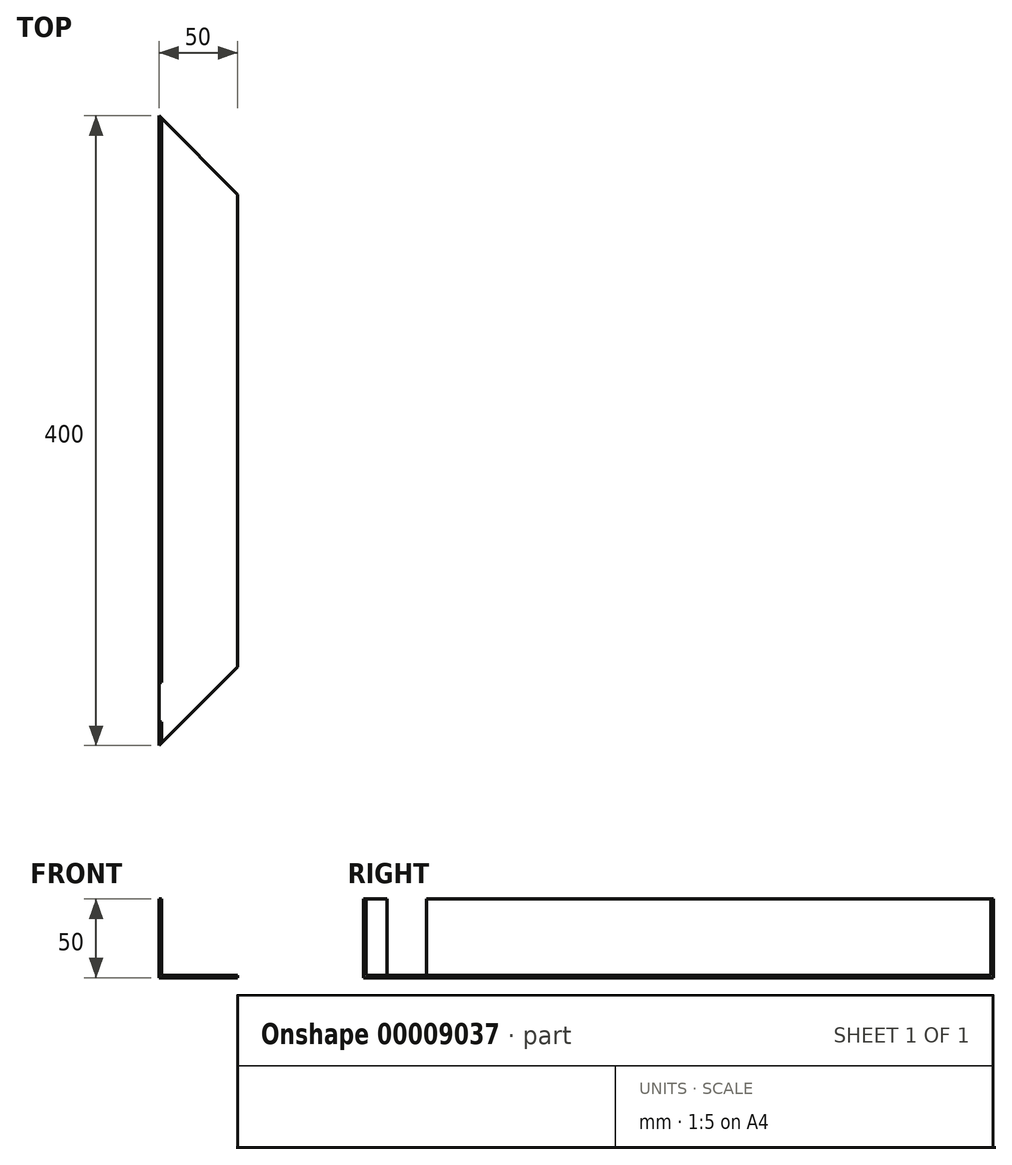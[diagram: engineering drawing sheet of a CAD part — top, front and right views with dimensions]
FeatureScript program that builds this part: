
annotation { "Feature Type Name" : "Feature", "Feature Type Description" : "" }
export const myFeature = defineFeature(function(context is Context, id is Id, definition is map)
    precondition{}
    {
        {
            var Q0;
            Q0=qCreatedBy(makeId("Front.planeOp"),FACE);
            var sketch = newSketch(context, id + "F0", { "sketchPlane" : qUnion([Q0])});
            skLineSegment(sketch, "E0.bottom", {"start": v(-33, 48.4) * mm, "end": v(-31.4, 48.4) * mm});
            skLineSegment(sketch, "E0.top", {"start": v(-33, -1.6) * mm, "end": v(-31.4, -1.6) * mm});
            skLineSegment(sketch, "E0.left", {"start": v(-33, 48.4) * mm, "end": v(-33, -1.6) * mm});
            skLineSegment(sketch, "E0.right", {"start": v(-31.4, 48.4) * mm, "end": v(-31.4, -1.6) * mm});
            skLineSegment(sketch, "E1.bottom", {"start": v(-33, -1.6) * mm, "end": v(17, -1.6) * mm});
            skLineSegment(sketch, "E1.top", {"start": v(-33, 0) * mm, "end": v(17, 0) * mm});
            skLineSegment(sketch, "E1.left", {"start": v(-33, -1.6) * mm, "end": v(-33, 0) * mm});
            skLineSegment(sketch, "E1.right", {"start": v(17, -1.6) * mm, "end": v(17, 0) * mm});
            skSolve(sketch);
        }
        {
            var Q0;
            Q0=qSketchRegion(id+"F0",true);
            extrude(context, id + "F1", {"entities" : qUnion([Q0]), "depth" : 400 * mm});
        }
        {
            var Q0;
            Q0=makeQuery(id+"F1.opExtrude","SWEPT_FACE",FACE,{"disambiguationData":[OSD([sQuery(id+"F0.wireOp",EDGE,"E1.bottom")])]});
            var sketch = newSketch(context, id + "F2", { "sketchPlane" : qUnion([Q0])});
            skLineSegment(sketch, "E2", {"start": v(-33, 0) * mm, "end": v(17, 50) * mm});
            skLineSegment(sketch, "E3", {"start": v(17, 50) * mm, "end": v(17, 0) * mm});
            skLineSegment(sketch, "E4", {"start": v(17, 0) * mm, "end": v(-33, 0) * mm});
            skSolve(sketch);
        }
        {
            var Q0;
            Q0=qSketchRegion(id+"F2",true);
            extrude(context, id + "F3", {"entities" : qUnion([Q0]), "operationType" : NewBodyOperationType.REMOVE, "endBound" : BoundingType.THROUGH_ALL, "oppositeDirection" : true, "depth" : 25 * mm});
        }
        {
            var Q0;
            Q0=makeQuery(id+"F1.opExtrude","SWEPT_FACE",FACE,{"disambiguationData":[OSD([sQuery(id+"F0.wireOp",EDGE,"E1.bottom")])]});
            var sketch = newSketch(context, id + "F4", { "sketchPlane" : qUnion([Q0])});
            skLineSegment(sketch, "E5", {"start": v(-33, 400) * mm, "end": v(17, 350) * mm});
            skLineSegment(sketch, "E6", {"start": v(17, 350) * mm, "end": v(17, 400) * mm});
            skLineSegment(sketch, "E7", {"start": v(17, 400) * mm, "end": v(-33, 400) * mm});
            skSolve(sketch);
        }
        {
            var Q0;
            Q0=qSketchRegion(id+"F4",true);
            extrude(context, id + "F5", {"entities" : qUnion([Q0]), "operationType" : NewBodyOperationType.REMOVE, "endBound" : BoundingType.THROUGH_ALL, "oppositeDirection" : true, "depth" : 25 * mm});
        }
        {
            var Q0;
            Q0=makeQuery(id+"F1.opExtrude","SWEPT_FACE",FACE,{"disambiguationData":[OSD([sQuery(id+"F0.wireOp",EDGE,"E0.left"),sQuery(id+"F0.wireOp",EDGE,"E1.left")])]});
            var sketch = newSketch(context, id + "F6", { "sketchPlane" : qUnion([Q0])});
            skLineSegment(sketch, "E8.bottom", {"start": v(385, 48.4) * mm, "end": v(360, 48.4) * mm});
            skLineSegment(sketch, "E9", {"start": v(360, 48.4) * mm, "end": v(360, 0) * mm});
            skLineSegment(sketch, "E10", {"start": v(385, 48.4) * mm, "end": v(385, 0) * mm});
            skLineSegment(sketch, "E11", {"start": v(385, 0) * mm, "end": v(360, 0) * mm});
            skSolve(sketch);
        }
        {
            var Q0;
            Q0 = qSketchRegion(id + "F6", true);
            extrude(context, id + "F7", {"entities" : qUnion([Q0]), "operationType" : NewBodyOperationType.REMOVE, "endBound" : BoundingType.THROUGH_ALL, "oppositeDirection" : true, "depth" : 25 * mm});
        }
    });
